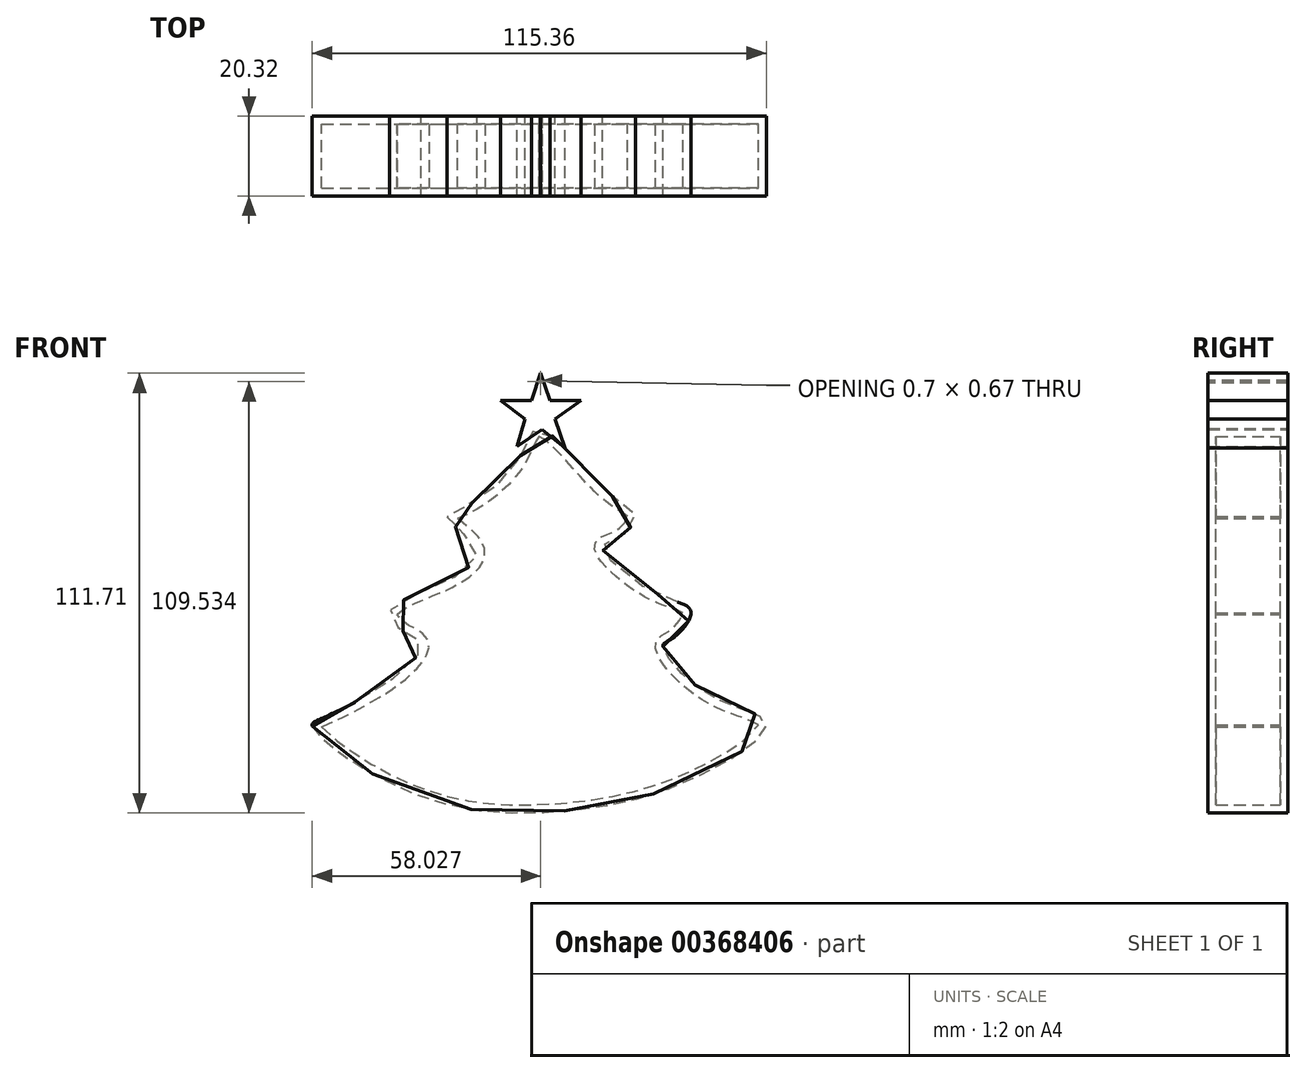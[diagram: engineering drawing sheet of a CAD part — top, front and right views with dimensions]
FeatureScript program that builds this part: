
annotation { "Feature Type Name" : "Feature", "Feature Type Description" : "" }
export const myFeature = defineFeature(function(context is Context, id is Id, definition is map)
    precondition{}
    {
        {
            var Q0;
            Q0=qCreatedBy(makeId("Front.planeOp"),FACE);
            var sketch = newSketch(context, id + "F0", { "sketchPlane" : qUnion([Q0])});
            skPoint(sketch, "E0.15.internal.snap0", {"position": v(1.13, 56.39) * mm});
            skFitSpline(sketch, "E0", {"points": [v(-56.53, -29.1) * mm, v(-32.06, -45.7) * mm, v(5.35, -50.76) * mm, v(39.1, -42.89) * mm, v(58.79, -28.54) * mm, v(48.38, -23.2) * mm, v(35.16, -13.36) * mm, v(32.63, -8.3) * mm, v(35.16, -6.6) * mm, v(39.66, 0) * mm, v(30.1, 4.92) * mm, v(17.16, 16.45) * mm, v(20.82, 18.42) * mm, v(25.6, 24.33) * mm, v(18.85, 29.95) * mm, v(1.13, 46.54) * mm, v(-4.21, 38.67) * mm, v(-18, 26.58) * mm, v(-22.21, 23.76) * mm, v(-14.9, 16.17) * mm, v(-21.93, 8.02) * mm, v(-36.84, 0) * mm, v(-33.46, -4.92) * mm, v(-28.96, -8.02) * mm, v(-34.87, -16.17) * mm, v(-54.28, -27.14) * mm, v(-56.53, -29.1) * mm]});
            skSolve(sketch);
        }
        {
            var Q0;
            Q0=qSketchRegion(id+"F0",true);
            extrude(context, id + "F1", {"entities" : qUnion([Q0]), "depth" : 20.32 * mm});
        }
        {
            var Q0;
            Q0=makeQuery(id+"F1.opExtrude","CAP_FACE",FACE,{"disambiguationData":[OSD([sQuery(id+"F0.wireOp",EDGE,"E0")])],"isStart":false});
            var Q1;
            Q1=makeQuery(id+"F1.opExtrude","SWEPT_BODY",BODY,{"disambiguationData":[OSD([sQuery(id+"F0.wireOp",EDGE,"E0")])]});
            shell(context, id + "F2", {"isHollow" : true, "entities" : qUnion([Q0]), "parts" : qUnion([Q1]), "thickness" : 2 * mm});
        }
        {
            var Q0;
            Q0=makeQuery(id+"F1.opExtrude","CAP_FACE",FACE,{"disambiguationData":[OSD([sQuery(id+"F0.wireOp",EDGE,"E0")])],"isStart":false});
            var sketch = newSketch(context, id + "F3", { "sketchPlane" : qUnion([Q0])});
            skLineSegment(sketch, "E1", {"start": v(-8.68, 53.61) * mm, "end": v(-0.89, 53.61) * mm});
            skLineSegment(sketch, "E2", {"start": v(-0.89, 53.61) * mm, "end": v(1.45, 60.62) * mm});
            skLineSegment(sketch, "E3", {"start": v(1.45, 60.62) * mm, "end": v(3.86, 53.7) * mm});
            skLineSegment(sketch, "E4", {"start": v(3.86, 53.7) * mm, "end": v(11.75, 53.7) * mm});
            skLineSegment(sketch, "E5", {"start": v(11.75, 53.7) * mm, "end": v(5.18, 48.94) * mm});
            skLineSegment(sketch, "E6", {"start": v(5.18, 48.94) * mm, "end": v(7.65, 41.6) * mm});
            skLineSegment(sketch, "E7", {"start": v(7.65, 41.6) * mm, "end": v(1.9, 46.37) * mm});
            skLineSegment(sketch, "E8", {"start": v(1.9, 46.37) * mm, "end": v(-4.57, 42) * mm});
            skLineSegment(sketch, "E9", {"start": v(-4.57, 42) * mm, "end": v(-2.54, 48.94) * mm});
            skLineSegment(sketch, "E10", {"start": v(-2.54, 48.94) * mm, "end": v(-8.68, 53.61) * mm});
            skSolve(sketch);
        }
        {
            var Q0;
            Q0=qSketchRegion(id+"F3",true);
            extrude(context, id + "F4", {"entities" : qUnion([Q0]), "depth" : 20.32 * mm});
        }
        {
            var Q0;
            Q0=makeQuery(id+"F4.opExtrude","SWEPT_BODY",BODY,{"disambiguationData":[OSD([sQuery(id+"F3.wireOp",EDGE,"E1"),sQuery(id+"F3.wireOp",EDGE,"E2"),sQuery(id+"F3.wireOp",EDGE,"E3"),sQuery(id+"F3.wireOp",EDGE,"E4"),sQuery(id+"F3.wireOp",EDGE,"E5"),sQuery(id+"F3.wireOp",EDGE,"E6"),sQuery(id+"F3.wireOp",EDGE,"E7"),sQuery(id+"F3.wireOp",EDGE,"E8"),sQuery(id+"F3.wireOp",EDGE,"E9"),sQuery(id+"F3.wireOp",EDGE,"E10")])]});
            var Q1;
            Q1=makeQuery(id+"F4.opExtrude","SWEPT_EDGE",EDGE,{"disambiguationData":[OSD([sQuery(id+"F0.wireOp",EDGE,"E0"),sQuery(id+"F3.wireOp",EDGE,"E6"),sQuery(id+"F3.wireOp",EDGE,"E7")])]});
            transform(context, id + "F5", {"entities" : qUnion([Q0]), "transformType" : TransformType.TRANSLATION_ENTITY, "oppositeDirectionEntity" : false, "transformLine" : qUnion([Q1]), "makeCopy" : false});
        }
        {
            var Q0;
            Q0=makeQuery(id+"F4.opExtrude","CAP_FACE",FACE,{"disambiguationData":[OSD([sQuery(id+"F3.wireOp",EDGE,"E1"),sQuery(id+"F3.wireOp",EDGE,"E2"),sQuery(id+"F3.wireOp",EDGE,"E3"),sQuery(id+"F3.wireOp",EDGE,"E4"),sQuery(id+"F3.wireOp",EDGE,"E5"),sQuery(id+"F3.wireOp",EDGE,"E6"),sQuery(id+"F3.wireOp",EDGE,"E7"),sQuery(id+"F3.wireOp",EDGE,"E8"),sQuery(id+"F3.wireOp",EDGE,"E9"),sQuery(id+"F3.wireOp",EDGE,"E10")])],"isStart":false});
            var sketch = newSketch(context, id + "F6", { "sketchPlane" : qUnion([Q0])});
            skLineSegment(sketch, "E11", {"start": v(1.12, 58.52) * mm, "end": v(1.38, 58.52) * mm});
            skLineSegment(sketch, "E12", {"start": v(1.38, 58.52) * mm, "end": v(1.46, 58.78) * mm});
            skLineSegment(sketch, "E13", {"start": v(1.46, 58.78) * mm, "end": v(1.54, 58.52) * mm});
            skLineSegment(sketch, "E14", {"start": v(1.54, 58.52) * mm, "end": v(1.82, 58.52) * mm});
            skLineSegment(sketch, "E15", {"start": v(1.82, 58.52) * mm, "end": v(1.6, 58.37) * mm});
            skLineSegment(sketch, "E16", {"start": v(1.6, 58.37) * mm, "end": v(1.68, 58.1) * mm});
            skLineSegment(sketch, "E17", {"start": v(1.68, 58.1) * mm, "end": v(1.46, 58.26) * mm});
            skLineSegment(sketch, "E18", {"start": v(1.46, 58.26) * mm, "end": v(1.24, 58.1) * mm});
            skLineSegment(sketch, "E19", {"start": v(1.24, 58.1) * mm, "end": v(1.32, 58.36) * mm});
            skLineSegment(sketch, "E20", {"start": v(1.32, 58.36) * mm, "end": v(1.12, 58.52) * mm});
            skSolve(sketch);
        }
        {
            var Q0;
            Q0=qSketchRegion(id+"F6",true);
            extrude(context, id + "F7", {"entities" : qUnion([Q0]), "operationType" : NewBodyOperationType.REMOVE, "oppositeDirection" : true, "depth" : 25.4 * mm});
        }
    });
